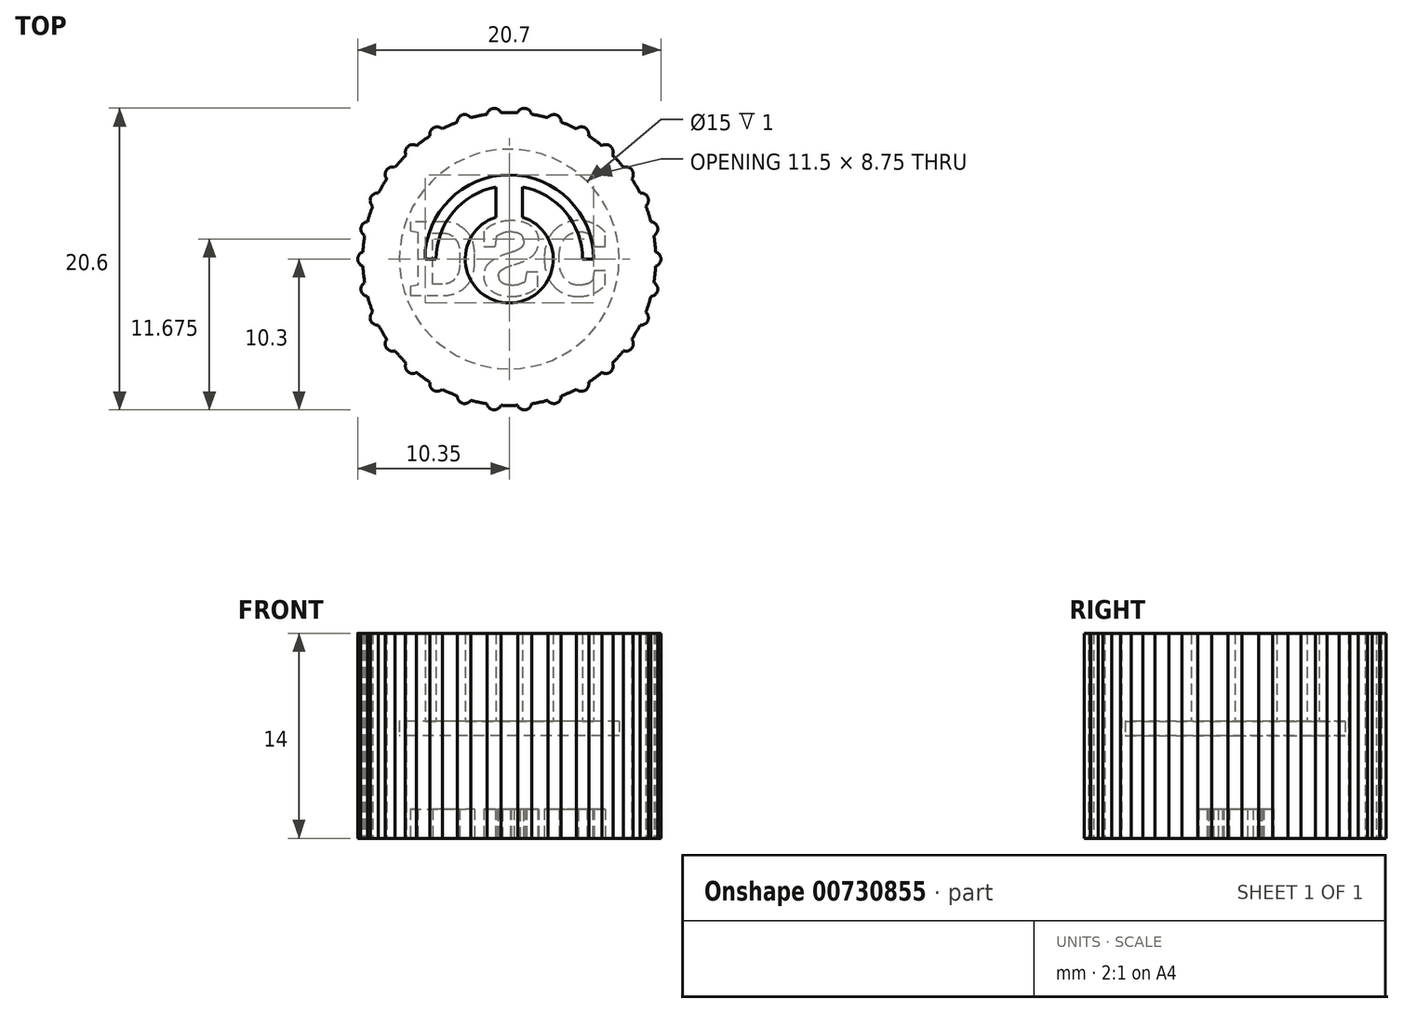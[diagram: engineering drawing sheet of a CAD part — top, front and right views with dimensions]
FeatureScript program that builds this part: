
annotation { "Feature Type Name" : "Feature", "Feature Type Description" : "" }
export const myFeature = defineFeature(function(context is Context, id is Id, definition is map)
    precondition{}
    {
        {
            var Q0;
            Q0=qCreatedBy(makeId("Top.planeOp"),FACE);
            var sketch = newSketch(context, id + "F0", { "sketchPlane" : qUnion([Q0])});
            skArc(sketch, "E0", {"start": v(-0.9, 2.86) * mm, "mid": v(0, -3) * mm, "end": v(0.9, 2.86) * mm});
            skArc(sketch, "E1", {"start": v(-0.9, 4.92) * mm, "mid": v(-3.84, 3.2) * mm, "end": v(-5, 0) * mm});
            skArc(sketch, "E2", {"start": v(5.75, 0) * mm, "mid": v(0, 5.75) * mm, "end": v(-5.75, 0) * mm});
            skArc(sketch, "E3", {"start": v(-9.99, -0.48) * mm, "mid": v(-9.95, -1.05) * mm, "end": v(-9.87, -1.6) * mm});
            skLineSegment(sketch, "E4", {"start": v(-0.9, 2.86) * mm, "end": v(-0.9, 4.92) * mm});
            skLineSegment(sketch, "E5", {"start": v(0.9, 4.92) * mm, "end": v(0.9, 2.86) * mm});
            skLineSegment(sketch, "E6", {"start": v(-5.75, 0) * mm, "end": v(-5, 0) * mm});
            skLineSegment(sketch, "E7.trimOffspring", {"start": v(5, 0) * mm, "end": v(5.75, 0) * mm});
            skArc(sketch, "E8.trimOffspring", {"start": v(5, 0) * mm, "mid": v(3.84, 3.2) * mm, "end": v(0.9, 4.92) * mm});
            skArc(sketch, "E9", {"start": v(-9.99, 0.48) * mm, "mid": v(-10.35, 0) * mm, "end": v(-9.99, -0.48) * mm});
            skArc(sketch, "E10.1.0", {"start": v(-9.87, -1.6) * mm, "mid": v(-10.12, -2.15) * mm, "end": v(-9.67, -2.55) * mm});
            skArc(sketch, "E10.2.0", {"start": v(-9.32, -3.62) * mm, "mid": v(-9.46, -4.21) * mm, "end": v(-8.93, -4.5) * mm});
            skArc(sketch, "E10.3.0", {"start": v(-8.36, -5.48) * mm, "mid": v(-8.37, -6.08) * mm, "end": v(-7.8, -6.26) * mm});
            skArc(sketch, "E10.4.0", {"start": v(-7.04, -7.1) * mm, "mid": v(-6.93, -7.7) * mm, "end": v(-6.33, -7.74) * mm});
            skArc(sketch, "E10.5.0", {"start": v(-5.41, -8.4) * mm, "mid": v(-5.18, -8.96) * mm, "end": v(-4.58, -8.9) * mm});
            skArc(sketch, "E10.6.0", {"start": v(-3.54, -9.35) * mm, "mid": v(-3.2, -9.84) * mm, "end": v(-2.63, -9.65) * mm});
            skArc(sketch, "E10.7.0", {"start": v(-1.52, -9.88) * mm, "mid": v(-1.08, -10.3) * mm, "end": v(-0.57, -9.98) * mm});
            skArc(sketch, "E10.8.0", {"start": v(0.57, -9.98) * mm, "mid": v(1.08, -10.3) * mm, "end": v(1.52, -9.88) * mm});
            skArc(sketch, "E10.9.0", {"start": v(2.63, -9.65) * mm, "mid": v(3.2, -9.84) * mm, "end": v(3.54, -9.35) * mm});
            skArc(sketch, "E10.10.0", {"start": v(4.58, -8.9) * mm, "mid": v(5.18, -8.96) * mm, "end": v(5.41, -8.4) * mm});
            skArc(sketch, "E10.11.0", {"start": v(6.33, -7.74) * mm, "mid": v(6.93, -7.7) * mm, "end": v(7.04, -7.1) * mm});
            skArc(sketch, "E10.12.0", {"start": v(7.8, -6.26) * mm, "mid": v(8.37, -6.08) * mm, "end": v(8.36, -5.48) * mm});
            skArc(sketch, "E10.13.0", {"start": v(8.93, -4.5) * mm, "mid": v(9.46, -4.21) * mm, "end": v(9.32, -3.62) * mm});
            skArc(sketch, "E10.14.0", {"start": v(9.67, -2.55) * mm, "mid": v(10.12, -2.15) * mm, "end": v(9.87, -1.6) * mm});
            skArc(sketch, "E10.15.0", {"start": v(9.99, -0.48) * mm, "mid": v(10.35, 0) * mm, "end": v(9.99, 0.48) * mm});
            skArc(sketch, "E10.16.0", {"start": v(9.87, 1.6) * mm, "mid": v(10.12, 2.15) * mm, "end": v(9.67, 2.55) * mm});
            skArc(sketch, "E10.17.0", {"start": v(9.32, 3.62) * mm, "mid": v(9.46, 4.21) * mm, "end": v(8.93, 4.5) * mm});
            skArc(sketch, "E10.18.0", {"start": v(8.36, 5.48) * mm, "mid": v(8.37, 6.08) * mm, "end": v(7.8, 6.26) * mm});
            skArc(sketch, "E10.19.0", {"start": v(7.04, 7.1) * mm, "mid": v(6.93, 7.7) * mm, "end": v(6.33, 7.74) * mm});
            skArc(sketch, "E10.20.0", {"start": v(5.41, 8.4) * mm, "mid": v(5.18, 8.96) * mm, "end": v(4.58, 8.9) * mm});
            skArc(sketch, "E10.21.0", {"start": v(3.54, 9.35) * mm, "mid": v(3.2, 9.84) * mm, "end": v(2.63, 9.65) * mm});
            skArc(sketch, "E10.22.0", {"start": v(1.52, 9.88) * mm, "mid": v(1.08, 10.3) * mm, "end": v(0.57, 9.98) * mm});
            skArc(sketch, "E10.23.0", {"start": v(-0.57, 9.98) * mm, "mid": v(-1.08, 10.3) * mm, "end": v(-1.52, 9.88) * mm});
            skArc(sketch, "E10.24.0", {"start": v(-2.63, 9.65) * mm, "mid": v(-3.2, 9.84) * mm, "end": v(-3.54, 9.35) * mm});
            skArc(sketch, "E10.25.0", {"start": v(-4.58, 8.9) * mm, "mid": v(-5.18, 8.96) * mm, "end": v(-5.41, 8.4) * mm});
            skArc(sketch, "E10.26.0", {"start": v(-6.33, 7.74) * mm, "mid": v(-6.93, 7.7) * mm, "end": v(-7.04, 7.1) * mm});
            skArc(sketch, "E10.27.0", {"start": v(-7.8, 6.26) * mm, "mid": v(-8.37, 6.08) * mm, "end": v(-8.36, 5.48) * mm});
            skArc(sketch, "E10.28.0", {"start": v(-8.93, 4.5) * mm, "mid": v(-9.46, 4.21) * mm, "end": v(-9.32, 3.62) * mm});
            skArc(sketch, "E10.29.0", {"start": v(-9.67, 2.55) * mm, "mid": v(-10.12, 2.15) * mm, "end": v(-9.87, 1.6) * mm});
            skArc(sketch, "E11.trimOffspring", {"start": v(-9.87, 1.6) * mm, "mid": v(-9.95, 1.05) * mm, "end": v(-9.99, 0.48) * mm});
            skArc(sketch, "E12.trimOffspring", {"start": v(-9.32, 3.62) * mm, "mid": v(-9.51, 3.1) * mm, "end": v(-9.67, 2.55) * mm});
            skArc(sketch, "E13.trimOffspring", {"start": v(-8.36, 5.48) * mm, "mid": v(-8.66, 5) * mm, "end": v(-8.93, 4.5) * mm});
            skArc(sketch, "E14.trimOffspring", {"start": v(-7.04, 7.1) * mm, "mid": v(-7.43, 6.7) * mm, "end": v(-7.8, 6.26) * mm});
            skArc(sketch, "E15.trimOffspring", {"start": v(-5.41, 8.4) * mm, "mid": v(-5.88, 8.1) * mm, "end": v(-6.33, 7.74) * mm});
            skArc(sketch, "E16.trimOffspring", {"start": v(-3.54, 9.35) * mm, "mid": v(-4.07, 9.14) * mm, "end": v(-4.58, 8.9) * mm});
            skArc(sketch, "E17.trimOffspring", {"start": v(-1.52, 9.88) * mm, "mid": v(-2.08, 9.78) * mm, "end": v(-2.63, 9.65) * mm});
            skArc(sketch, "E18.trimOffspring", {"start": v(0.57, 9.98) * mm, "mid": v(0, 10) * mm, "end": v(-0.57, 9.98) * mm});
            skArc(sketch, "E19.trimOffspring", {"start": v(2.63, 9.65) * mm, "mid": v(2.08, 9.78) * mm, "end": v(1.52, 9.88) * mm});
            skArc(sketch, "E20.trimOffspring", {"start": v(4.58, 8.9) * mm, "mid": v(4.07, 9.14) * mm, "end": v(3.54, 9.35) * mm});
            skArc(sketch, "E21.trimOffspring", {"start": v(6.33, 7.74) * mm, "mid": v(5.88, 8.1) * mm, "end": v(5.41, 8.4) * mm});
            skArc(sketch, "E22.trimOffspring", {"start": v(7.8, 6.26) * mm, "mid": v(7.43, 6.7) * mm, "end": v(7.04, 7.1) * mm});
            skArc(sketch, "E23.trimOffspring", {"start": v(8.93, 4.5) * mm, "mid": v(8.66, 5) * mm, "end": v(8.36, 5.48) * mm});
            skArc(sketch, "E24.trimOffspring", {"start": v(9.67, 2.55) * mm, "mid": v(9.51, 3.1) * mm, "end": v(9.32, 3.62) * mm});
            skArc(sketch, "E25.trimOffspring", {"start": v(9.99, 0.48) * mm, "mid": v(9.95, 1.05) * mm, "end": v(9.87, 1.6) * mm});
            skArc(sketch, "E26.trimOffspring", {"start": v(9.87, -1.6) * mm, "mid": v(9.95, -1.05) * mm, "end": v(9.99, -0.48) * mm});
            skArc(sketch, "E27.trimOffspring", {"start": v(8.36, -5.48) * mm, "mid": v(9.14, -4.07) * mm, "end": v(9.67, -2.55) * mm});
            skArc(sketch, "E28.trimOffspring", {"start": v(7.04, -7.1) * mm, "mid": v(7.43, -6.7) * mm, "end": v(7.8, -6.26) * mm});
            skArc(sketch, "E29.trimOffspring", {"start": v(5.41, -8.4) * mm, "mid": v(5.88, -8.1) * mm, "end": v(6.33, -7.74) * mm});
            skArc(sketch, "E30.trimOffspring", {"start": v(3.54, -9.35) * mm, "mid": v(4.07, -9.14) * mm, "end": v(4.58, -8.9) * mm});
            skArc(sketch, "E31.trimOffspring", {"start": v(1.52, -9.88) * mm, "mid": v(2.08, -9.78) * mm, "end": v(2.63, -9.65) * mm});
            skArc(sketch, "E32.trimOffspring", {"start": v(-0.57, -9.98) * mm, "mid": v(0, -10) * mm, "end": v(0.57, -9.98) * mm});
            skArc(sketch, "E33.trimOffspring", {"start": v(-2.63, -9.65) * mm, "mid": v(-2.08, -9.78) * mm, "end": v(-1.52, -9.88) * mm});
            skArc(sketch, "E34.trimOffspring", {"start": v(-4.58, -8.9) * mm, "mid": v(-4.07, -9.14) * mm, "end": v(-3.54, -9.35) * mm});
            skArc(sketch, "E35.trimOffspring", {"start": v(-6.33, -7.74) * mm, "mid": v(-5.88, -8.1) * mm, "end": v(-5.41, -8.4) * mm});
            skArc(sketch, "E36.trimOffspring", {"start": v(-7.8, -6.26) * mm, "mid": v(-7.43, -6.7) * mm, "end": v(-7.04, -7.1) * mm});
            skArc(sketch, "E37.trimOffspring", {"start": v(-8.93, -4.5) * mm, "mid": v(-8.66, -5) * mm, "end": v(-8.36, -5.48) * mm});
            skArc(sketch, "E38.trimOffspring", {"start": v(-9.67, -2.55) * mm, "mid": v(-9.51, -3.1) * mm, "end": v(-9.32, -3.62) * mm});
            skSolve(sketch);
        }
        {
            var Q0;
            Q0=qCreatedBy(makeId("Top.planeOp"),FACE);
            cPlane(context, id + "F1", {"entities" : qUnion([Q0]), "cplaneType" : CPlaneType.OFFSET, "offset" : 6 * mm, "width" : 150 * mm, "height" : 150 * mm});
        }
        {
            var Q0;
            Q0=qCreatedBy(makeId("Top.planeOp"),FACE);
            cPlane(context, id + "F2", {"entities" : qUnion([Q0]), "cplaneType" : CPlaneType.OFFSET, "offset" : 14 * mm, "oppositeDirection" : true, "width" : 150 * mm, "height" : 150 * mm});
        }
        {
            var Q0;
            Q0 = qSketchRegion(id + "F0", true);
            var Q1;
            Q1=qCreatedBy(id+"F1.planeOp",FACE);
            var Q2;
            Q2=qCreatedBy(id+"F2.planeOp",FACE);
            extrude(context, id + "F3", {"entities" : qUnion([Q0]), "endBound" : BoundingType.UP_TO_SURFACE, "depth" : 25 * mm, "endBoundEntityFace" : qUnion([Q1]), "offsetDistance" : 25 * mm});
        }
        {
            var Q0;
            Q0=makeQuery(id+"F3.opExtrude","CAP_FACE",FACE,{"disambiguationData":[OSD([sQuery(id+"F0.wireOp",EDGE,"E0"),sQuery(id+"F0.wireOp",EDGE,"E1"),sQuery(id+"F0.wireOp",EDGE,"E2"),sQuery(id+"F0.wireOp",EDGE,"E3"),sQuery(id+"F0.wireOp",EDGE,"E4"),sQuery(id+"F0.wireOp",EDGE,"E5"),sQuery(id+"F0.wireOp",EDGE,"E6"),sQuery(id+"F0.wireOp",EDGE,"E7.trimOffspring"),sQuery(id+"F0.wireOp",EDGE,"E8.trimOffspring"),sQuery(id+"F0.wireOp",EDGE,"E9"),sQuery(id+"F0.wireOp",EDGE,"E10.1.0"),sQuery(id+"F0.wireOp",EDGE,"E10.2.0"),sQuery(id+"F0.wireOp",EDGE,"E10.3.0"),sQuery(id+"F0.wireOp",EDGE,"E10.4.0"),sQuery(id+"F0.wireOp",EDGE,"E10.5.0"),sQuery(id+"F0.wireOp",EDGE,"E10.6.0"),sQuery(id+"F0.wireOp",EDGE,"E10.7.0"),sQuery(id+"F0.wireOp",EDGE,"E10.8.0"),sQuery(id+"F0.wireOp",EDGE,"E10.9.0"),sQuery(id+"F0.wireOp",EDGE,"E10.10.0"),sQuery(id+"F0.wireOp",EDGE,"E10.11.0"),sQuery(id+"F0.wireOp",EDGE,"E10.12.0"),sQuery(id+"F0.wireOp",EDGE,"E10.13.0"),sQuery(id+"F0.wireOp",EDGE,"E10.14.0"),sQuery(id+"F0.wireOp",EDGE,"E10.15.0"),sQuery(id+"F0.wireOp",EDGE,"E10.16.0"),sQuery(id+"F0.wireOp",EDGE,"E10.17.0"),sQuery(id+"F0.wireOp",EDGE,"E10.18.0"),sQuery(id+"F0.wireOp",EDGE,"E10.19.0"),sQuery(id+"F0.wireOp",EDGE,"E10.20.0"),sQuery(id+"F0.wireOp",EDGE,"E10.21.0"),sQuery(id+"F0.wireOp",EDGE,"E10.22.0"),sQuery(id+"F0.wireOp",EDGE,"E10.23.0"),sQuery(id+"F0.wireOp",EDGE,"E10.24.0"),sQuery(id+"F0.wireOp",EDGE,"E10.25.0"),sQuery(id+"F0.wireOp",EDGE,"E10.26.0"),sQuery(id+"F0.wireOp",EDGE,"E10.27.0"),sQuery(id+"F0.wireOp",EDGE,"E10.28.0"),sQuery(id+"F0.wireOp",EDGE,"E10.29.0"),sQuery(id+"F0.wireOp",EDGE,"E11.trimOffspring"),sQuery(id+"F0.wireOp",EDGE,"E12.trimOffspring"),sQuery(id+"F0.wireOp",EDGE,"E13.trimOffspring"),sQuery(id+"F0.wireOp",EDGE,"E14.trimOffspring"),sQuery(id+"F0.wireOp",EDGE,"E15.trimOffspring"),sQuery(id+"F0.wireOp",EDGE,"E16.trimOffspring"),sQuery(id+"F0.wireOp",EDGE,"E17.trimOffspring"),sQuery(id+"F0.wireOp",EDGE,"E18.trimOffspring"),sQuery(id+"F0.wireOp",EDGE,"E19.trimOffspring"),sQuery(id+"F0.wireOp",EDGE,"E20.trimOffspring"),sQuery(id+"F0.wireOp",EDGE,"E21.trimOffspring"),sQuery(id+"F0.wireOp",EDGE,"E22.trimOffspring"),sQuery(id+"F0.wireOp",EDGE,"E23.trimOffspring"),sQuery(id+"F0.wireOp",EDGE,"E24.trimOffspring"),sQuery(id+"F0.wireOp",EDGE,"E25.trimOffspring"),sQuery(id+"F0.wireOp",EDGE,"E26.trimOffspring"),sQuery(id+"F0.wireOp",EDGE,"E27.trimOffspring"),sQuery(id+"F0.wireOp",EDGE,"E28.trimOffspring"),sQuery(id+"F0.wireOp",EDGE,"E29.trimOffspring"),sQuery(id+"F0.wireOp",EDGE,"E30.trimOffspring"),sQuery(id+"F0.wireOp",EDGE,"E31.trimOffspring"),sQuery(id+"F0.wireOp",EDGE,"E32.trimOffspring"),sQuery(id+"F0.wireOp",EDGE,"E33.trimOffspring"),sQuery(id+"F0.wireOp",EDGE,"E34.trimOffspring"),sQuery(id+"F0.wireOp",EDGE,"E35.trimOffspring"),sQuery(id+"F0.wireOp",EDGE,"E36.trimOffspring"),sQuery(id+"F0.wireOp",EDGE,"E37.trimOffspring"),sQuery(id+"F0.wireOp",EDGE,"E38.trimOffspring")])],"isStart":true});
            var sketch = newSketch(context, id + "F4", { "sketchPlane" : qUnion([Q0])});
            skArc(sketch, "E39", {"start": v(-9.99, -0.48) * mm, "mid": v(-9.95, -1.05) * mm, "end": v(-9.87, -1.6) * mm});
            skArc(sketch, "E40", {"start": v(-9.99, 0.48) * mm, "mid": v(-10.35, 0) * mm, "end": v(-9.99, -0.48) * mm});
            skArc(sketch, "E41.1.0", {"start": v(-9.87, -1.6) * mm, "mid": v(-10.12, -2.15) * mm, "end": v(-9.67, -2.55) * mm});
            skArc(sketch, "E41.2.0", {"start": v(-9.32, -3.62) * mm, "mid": v(-9.46, -4.21) * mm, "end": v(-8.93, -4.5) * mm});
            skArc(sketch, "E41.3.0", {"start": v(-8.36, -5.48) * mm, "mid": v(-8.37, -6.08) * mm, "end": v(-7.8, -6.26) * mm});
            skArc(sketch, "E41.4.0", {"start": v(-7.04, -7.1) * mm, "mid": v(-6.93, -7.7) * mm, "end": v(-6.33, -7.74) * mm});
            skArc(sketch, "E41.5.0", {"start": v(-5.41, -8.4) * mm, "mid": v(-5.18, -8.96) * mm, "end": v(-4.58, -8.9) * mm});
            skArc(sketch, "E41.6.0", {"start": v(-3.54, -9.35) * mm, "mid": v(-3.2, -9.84) * mm, "end": v(-2.63, -9.65) * mm});
            skArc(sketch, "E41.7.0", {"start": v(-1.52, -9.88) * mm, "mid": v(-1.08, -10.3) * mm, "end": v(-0.57, -9.98) * mm});
            skArc(sketch, "E41.8.0", {"start": v(0.57, -9.98) * mm, "mid": v(1.08, -10.3) * mm, "end": v(1.52, -9.88) * mm});
            skArc(sketch, "E41.9.0", {"start": v(2.63, -9.65) * mm, "mid": v(3.2, -9.84) * mm, "end": v(3.54, -9.35) * mm});
            skArc(sketch, "E41.10.0", {"start": v(4.58, -8.9) * mm, "mid": v(5.18, -8.96) * mm, "end": v(5.41, -8.4) * mm});
            skArc(sketch, "E41.11.0", {"start": v(6.33, -7.74) * mm, "mid": v(6.93, -7.7) * mm, "end": v(7.04, -7.1) * mm});
            skArc(sketch, "E41.12.0", {"start": v(7.8, -6.26) * mm, "mid": v(8.37, -6.08) * mm, "end": v(8.36, -5.48) * mm});
            skArc(sketch, "E41.13.0", {"start": v(8.93, -4.5) * mm, "mid": v(9.46, -4.21) * mm, "end": v(9.32, -3.62) * mm});
            skArc(sketch, "E41.14.0", {"start": v(9.67, -2.55) * mm, "mid": v(10.12, -2.15) * mm, "end": v(9.87, -1.6) * mm});
            skArc(sketch, "E41.15.0", {"start": v(9.99, -0.48) * mm, "mid": v(10.35, 0) * mm, "end": v(9.99, 0.48) * mm});
            skArc(sketch, "E41.16.0", {"start": v(9.87, 1.6) * mm, "mid": v(10.12, 2.15) * mm, "end": v(9.67, 2.55) * mm});
            skArc(sketch, "E41.17.0", {"start": v(9.32, 3.62) * mm, "mid": v(9.46, 4.21) * mm, "end": v(8.93, 4.5) * mm});
            skArc(sketch, "E41.18.0", {"start": v(8.36, 5.48) * mm, "mid": v(8.37, 6.08) * mm, "end": v(7.8, 6.26) * mm});
            skArc(sketch, "E41.19.0", {"start": v(7.04, 7.1) * mm, "mid": v(6.93, 7.7) * mm, "end": v(6.33, 7.74) * mm});
            skArc(sketch, "E41.20.0", {"start": v(5.41, 8.4) * mm, "mid": v(5.18, 8.96) * mm, "end": v(4.58, 8.9) * mm});
            skArc(sketch, "E41.21.0", {"start": v(3.54, 9.35) * mm, "mid": v(3.2, 9.84) * mm, "end": v(2.63, 9.65) * mm});
            skArc(sketch, "E41.22.0", {"start": v(1.52, 9.88) * mm, "mid": v(1.08, 10.3) * mm, "end": v(0.57, 9.98) * mm});
            skArc(sketch, "E41.23.0", {"start": v(-0.57, 9.98) * mm, "mid": v(-1.08, 10.3) * mm, "end": v(-1.52, 9.88) * mm});
            skArc(sketch, "E41.24.0", {"start": v(-2.63, 9.65) * mm, "mid": v(-3.2, 9.84) * mm, "end": v(-3.54, 9.35) * mm});
            skArc(sketch, "E41.25.0", {"start": v(-4.58, 8.9) * mm, "mid": v(-5.18, 8.96) * mm, "end": v(-5.41, 8.4) * mm});
            skArc(sketch, "E41.26.0", {"start": v(-6.33, 7.74) * mm, "mid": v(-6.93, 7.7) * mm, "end": v(-7.04, 7.1) * mm});
            skArc(sketch, "E41.27.0", {"start": v(-7.8, 6.26) * mm, "mid": v(-8.37, 6.08) * mm, "end": v(-8.36, 5.48) * mm});
            skArc(sketch, "E41.28.0", {"start": v(-8.93, 4.5) * mm, "mid": v(-9.46, 4.21) * mm, "end": v(-9.32, 3.62) * mm});
            skArc(sketch, "E41.29.0", {"start": v(-9.67, 2.55) * mm, "mid": v(-10.12, 2.15) * mm, "end": v(-9.87, 1.6) * mm});
            skArc(sketch, "E42.trimOffspring", {"start": v(-9.87, 1.6) * mm, "mid": v(-9.95, 1.05) * mm, "end": v(-9.99, 0.48) * mm});
            skArc(sketch, "E43.trimOffspring", {"start": v(-9.32, 3.62) * mm, "mid": v(-9.51, 3.1) * mm, "end": v(-9.67, 2.55) * mm});
            skArc(sketch, "E44.trimOffspring", {"start": v(-8.36, 5.48) * mm, "mid": v(-8.66, 5) * mm, "end": v(-8.93, 4.5) * mm});
            skArc(sketch, "E45.trimOffspring", {"start": v(-7.04, 7.1) * mm, "mid": v(-7.43, 6.7) * mm, "end": v(-7.8, 6.26) * mm});
            skArc(sketch, "E46.trimOffspring", {"start": v(-5.41, 8.4) * mm, "mid": v(-5.88, 8.1) * mm, "end": v(-6.33, 7.74) * mm});
            skArc(sketch, "E47.trimOffspring", {"start": v(-3.54, 9.35) * mm, "mid": v(-4.07, 9.14) * mm, "end": v(-4.58, 8.9) * mm});
            skArc(sketch, "E48.trimOffspring", {"start": v(-1.52, 9.88) * mm, "mid": v(-2.08, 9.78) * mm, "end": v(-2.63, 9.65) * mm});
            skArc(sketch, "E49.trimOffspring", {"start": v(0.57, 9.98) * mm, "mid": v(0, 10) * mm, "end": v(-0.57, 9.98) * mm});
            skArc(sketch, "E50.trimOffspring", {"start": v(2.63, 9.65) * mm, "mid": v(2.08, 9.78) * mm, "end": v(1.52, 9.88) * mm});
            skArc(sketch, "E51.trimOffspring", {"start": v(4.58, 8.9) * mm, "mid": v(4.07, 9.14) * mm, "end": v(3.54, 9.35) * mm});
            skArc(sketch, "E52.trimOffspring", {"start": v(6.33, 7.74) * mm, "mid": v(5.88, 8.1) * mm, "end": v(5.41, 8.4) * mm});
            skArc(sketch, "E53.trimOffspring", {"start": v(7.8, 6.26) * mm, "mid": v(7.43, 6.7) * mm, "end": v(7.04, 7.1) * mm});
            skArc(sketch, "E54.trimOffspring", {"start": v(8.93, 4.5) * mm, "mid": v(8.66, 5) * mm, "end": v(8.36, 5.48) * mm});
            skArc(sketch, "E55.trimOffspring", {"start": v(9.67, 2.55) * mm, "mid": v(9.51, 3.1) * mm, "end": v(9.32, 3.62) * mm});
            skArc(sketch, "E56.trimOffspring", {"start": v(9.99, 0.48) * mm, "mid": v(9.95, 1.05) * mm, "end": v(9.87, 1.6) * mm});
            skArc(sketch, "E57.trimOffspring", {"start": v(9.87, -1.6) * mm, "mid": v(9.95, -1.05) * mm, "end": v(9.99, -0.48) * mm});
            skArc(sketch, "E58.trimOffspring", {"start": v(8.36, -5.48) * mm, "mid": v(9.14, -4.07) * mm, "end": v(9.67, -2.55) * mm});
            skArc(sketch, "E59.trimOffspring", {"start": v(7.04, -7.1) * mm, "mid": v(7.43, -6.7) * mm, "end": v(7.8, -6.26) * mm});
            skArc(sketch, "E60.trimOffspring", {"start": v(5.41, -8.4) * mm, "mid": v(5.88, -8.1) * mm, "end": v(6.33, -7.74) * mm});
            skArc(sketch, "E61.trimOffspring", {"start": v(3.54, -9.35) * mm, "mid": v(4.07, -9.14) * mm, "end": v(4.58, -8.9) * mm});
            skArc(sketch, "E62.trimOffspring", {"start": v(1.52, -9.88) * mm, "mid": v(2.08, -9.78) * mm, "end": v(2.63, -9.65) * mm});
            skArc(sketch, "E63.trimOffspring", {"start": v(-0.57, -9.98) * mm, "mid": v(0, -10) * mm, "end": v(0.57, -9.98) * mm});
            skArc(sketch, "E64.trimOffspring", {"start": v(-2.63, -9.65) * mm, "mid": v(-2.08, -9.78) * mm, "end": v(-1.52, -9.88) * mm});
            skArc(sketch, "E65.trimOffspring", {"start": v(-4.58, -8.9) * mm, "mid": v(-4.07, -9.14) * mm, "end": v(-3.54, -9.35) * mm});
            skArc(sketch, "E66.trimOffspring", {"start": v(-6.33, -7.74) * mm, "mid": v(-5.88, -8.1) * mm, "end": v(-5.41, -8.4) * mm});
            skArc(sketch, "E67.trimOffspring", {"start": v(-7.8, -6.26) * mm, "mid": v(-7.43, -6.7) * mm, "end": v(-7.04, -7.1) * mm});
            skArc(sketch, "E68.trimOffspring", {"start": v(-8.93, -4.5) * mm, "mid": v(-8.66, -5) * mm, "end": v(-8.36, -5.48) * mm});
            skArc(sketch, "E69.trimOffspring", {"start": v(-9.67, -2.55) * mm, "mid": v(-9.51, -3.1) * mm, "end": v(-9.32, -3.62) * mm});
            skSolve(sketch);
        }
        {
            var Q0;
            Q0 = qSketchRegion(id + "F4", true);
            extrude(context, id + "F5", {"entities" : qUnion([Q0]), "operationType" : NewBodyOperationType.ADD, "depth" : 8 * mm, "offsetDistance" : 25 * mm});
        }
        {
            var Q0;
            Q0=makeQuery(id+"F5.opExtrude","CAP_FACE",FACE,{"disambiguationData":[OSD([sQuery(id+"F4.wireOp",EDGE,"E39"),sQuery(id+"F4.wireOp",EDGE,"E40"),sQuery(id+"F4.wireOp",EDGE,"E41.1.0"),sQuery(id+"F4.wireOp",EDGE,"E41.2.0"),sQuery(id+"F4.wireOp",EDGE,"E41.3.0"),sQuery(id+"F4.wireOp",EDGE,"E41.4.0"),sQuery(id+"F4.wireOp",EDGE,"E41.5.0"),sQuery(id+"F4.wireOp",EDGE,"E41.6.0"),sQuery(id+"F4.wireOp",EDGE,"E41.7.0"),sQuery(id+"F4.wireOp",EDGE,"E41.8.0"),sQuery(id+"F4.wireOp",EDGE,"E41.9.0"),sQuery(id+"F4.wireOp",EDGE,"E41.10.0"),sQuery(id+"F4.wireOp",EDGE,"E41.11.0"),sQuery(id+"F4.wireOp",EDGE,"E41.12.0"),sQuery(id+"F4.wireOp",EDGE,"E41.13.0"),sQuery(id+"F4.wireOp",EDGE,"E41.14.0"),sQuery(id+"F4.wireOp",EDGE,"E41.15.0"),sQuery(id+"F4.wireOp",EDGE,"E41.16.0"),sQuery(id+"F4.wireOp",EDGE,"E41.17.0"),sQuery(id+"F4.wireOp",EDGE,"E41.18.0"),sQuery(id+"F4.wireOp",EDGE,"E41.19.0"),sQuery(id+"F4.wireOp",EDGE,"E41.20.0"),sQuery(id+"F4.wireOp",EDGE,"E41.21.0"),sQuery(id+"F4.wireOp",EDGE,"E41.22.0"),sQuery(id+"F4.wireOp",EDGE,"E41.23.0"),sQuery(id+"F4.wireOp",EDGE,"E41.24.0"),sQuery(id+"F4.wireOp",EDGE,"E41.25.0"),sQuery(id+"F4.wireOp",EDGE,"E41.26.0"),sQuery(id+"F4.wireOp",EDGE,"E41.27.0"),sQuery(id+"F4.wireOp",EDGE,"E41.28.0"),sQuery(id+"F4.wireOp",EDGE,"E41.29.0"),sQuery(id+"F4.wireOp",EDGE,"E42.trimOffspring"),sQuery(id+"F4.wireOp",EDGE,"E43.trimOffspring"),sQuery(id+"F4.wireOp",EDGE,"E44.trimOffspring"),sQuery(id+"F4.wireOp",EDGE,"E45.trimOffspring"),sQuery(id+"F4.wireOp",EDGE,"E46.trimOffspring"),sQuery(id+"F4.wireOp",EDGE,"E47.trimOffspring"),sQuery(id+"F4.wireOp",EDGE,"E48.trimOffspring"),sQuery(id+"F4.wireOp",EDGE,"E49.trimOffspring"),sQuery(id+"F4.wireOp",EDGE,"E50.trimOffspring"),sQuery(id+"F4.wireOp",EDGE,"E51.trimOffspring"),sQuery(id+"F4.wireOp",EDGE,"E52.trimOffspring"),sQuery(id+"F4.wireOp",EDGE,"E53.trimOffspring"),sQuery(id+"F4.wireOp",EDGE,"E54.trimOffspring"),sQuery(id+"F4.wireOp",EDGE,"E55.trimOffspring"),sQuery(id+"F4.wireOp",EDGE,"E56.trimOffspring"),sQuery(id+"F4.wireOp",EDGE,"E57.trimOffspring"),sQuery(id+"F4.wireOp",EDGE,"E58.trimOffspring"),sQuery(id+"F4.wireOp",EDGE,"E59.trimOffspring"),sQuery(id+"F4.wireOp",EDGE,"E60.trimOffspring"),sQuery(id+"F4.wireOp",EDGE,"E61.trimOffspring"),sQuery(id+"F4.wireOp",EDGE,"E62.trimOffspring"),sQuery(id+"F4.wireOp",EDGE,"E63.trimOffspring"),sQuery(id+"F4.wireOp",EDGE,"E64.trimOffspring"),sQuery(id+"F4.wireOp",EDGE,"E65.trimOffspring"),sQuery(id+"F4.wireOp",EDGE,"E66.trimOffspring"),sQuery(id+"F4.wireOp",EDGE,"E67.trimOffspring"),sQuery(id+"F4.wireOp",EDGE,"E68.trimOffspring"),sQuery(id+"F4.wireOp",EDGE,"E69.trimOffspring")])],"isStart":false});
            var sketch = newSketch(context, id + "F6", { "sketchPlane" : qUnion([Q0])});
            skText(sketch, "E70", { "text": "DSC", "fontName": "RobotoSlab-Bold.ttf"});
            const initialGuessF6  = {"E70": [-0.00696, -0.00255, 1, 0, 0.0051]};
            skSetInitialGuess(sketch, initialGuessF6);
            skSolve(sketch);
        }
        {
            var Q0;
            Q0 = qSketchRegion(id + "F6", true);
            extrude(context, id + "F7", {"entities" : qUnion([Q0]), "operationType" : NewBodyOperationType.REMOVE, "oppositeDirection" : true, "depth" : 2 * mm, "offsetDistance" : 25 * mm});
        }
        {
            var Q0;
            Q0=qCreatedBy(makeId("Top.planeOp"),FACE);
            cPlane(context, id + "F8", {"entities" : qUnion([Q0]), "cplaneType" : CPlaneType.OFFSET, "offset" : 1 * mm, "oppositeDirection" : true, "width" : 150 * mm, "height" : 150 * mm});
        }
        {
            var Q0;
            Q0=qCreatedBy(id+"F8.planeOp",FACE);
            var sketch = newSketch(context, id + "F9", { "sketchPlane" : qUnion([Q0])});
            skCircle(sketch, "E71", {"center": v(0, 0) * mm, "radius": 7.5 * mm});
            skSolve(sketch);
        }
        {
            var Q0;
            Q0 = qSketchRegion(id + "F9", true);
            var Q1;
            Q1=sQuery(id+"F9.wireOp",EDGE,"E71");
            extrude(context, id + "F10", {"entities" : qUnion([Q0]), "operationType" : NewBodyOperationType.REMOVE, "surfaceEntities" : qUnion([Q1]), "depth" : 1 * mm, "offsetDistance" : 25 * mm});
        }
    });
